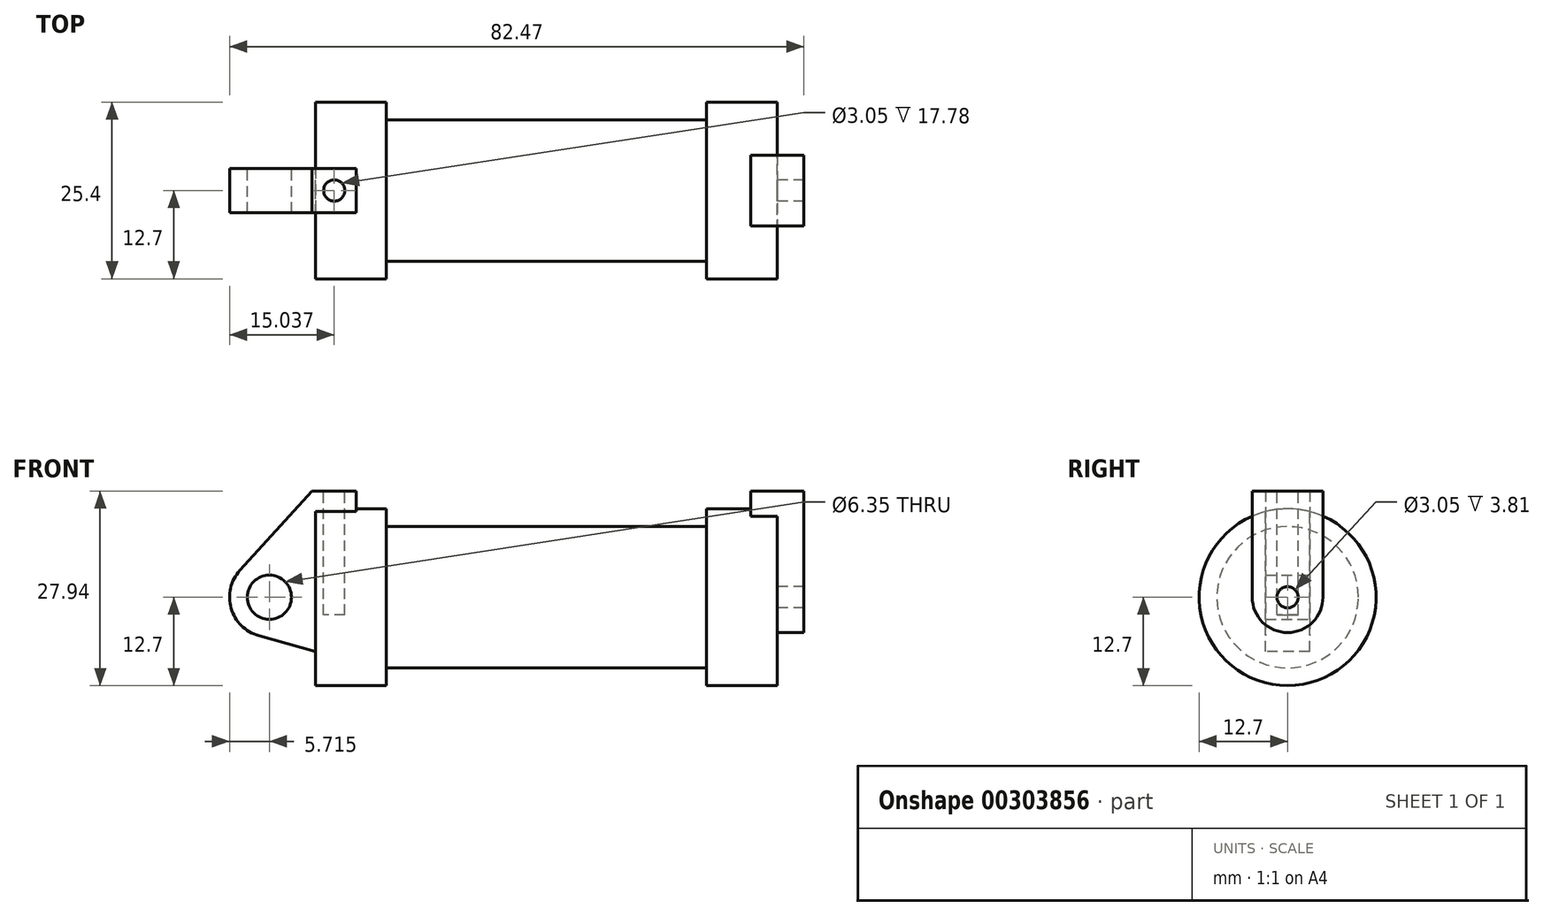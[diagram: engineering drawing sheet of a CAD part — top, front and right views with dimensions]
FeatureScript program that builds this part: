
annotation { "Feature Type Name" : "Feature", "Feature Type Description" : "" }
export const myFeature = defineFeature(function(context is Context, id is Id, definition is map)
    precondition{}
    {
        {
            var Q0;
            Q0=qCreatedBy(makeId("Front.planeOp"),FACE);
            var sketch = newSketch(context, id + "F0", { "sketchPlane" : qUnion([Q0])});
            skLineSegment(sketch, "E0", {"start": v(0, 0) * mm, "end": v(0, 12.7) * mm});
            skLineSegment(sketch, "E1", {"start": v(0, 12.7) * mm, "end": v(10.16, 12.7) * mm});
            skLineSegment(sketch, "E2", {"start": v(10.16, 12.7) * mm, "end": v(10.16, 10.16) * mm});
            skLineSegment(sketch, "E3", {"start": v(10.16, 10.16) * mm, "end": v(56.13, 10.16) * mm});
            skLineSegment(sketch, "E4", {"start": v(56.13, 10.16) * mm, "end": v(56.13, 12.7) * mm});
            skLineSegment(sketch, "E5", {"start": v(56.13, 12.7) * mm, "end": v(66.3, 12.7) * mm});
            skLineSegment(sketch, "E6", {"start": v(66.3, 12.7) * mm, "end": v(66.3, 0) * mm});
            skLineSegment(sketch, "E7", {"start": v(66.3, 0) * mm, "end": v(0, 0) * mm});
            skLineSegment(sketch, "E8", {"start": v(5.84, 15.24) * mm, "end": v(-0.5, 15.24) * mm});
            skLineSegment(sketch, "E9", {"start": v(-0.5, 15.24) * mm, "end": v(-10.88, 3.85) * mm});
            skLineSegment(sketch, "E10", {"start": v(0, 0) * mm, "end": v(-6.65, 0) * mm});
            skCircle(sketch, "E11", {"center": v(-6.65, 0) * mm, "radius": 5.72 * mm});
            skCircle(sketch, "E12", {"center": v(-6.65, 0) * mm, "radius": 3.18 * mm});
            skLineSegment(sketch, "E13", {"start": v(5.84, 15.24) * mm, "end": v(5.84, -9.4) * mm});
            skLineSegment(sketch, "E14", {"start": v(5.84, -9.4) * mm, "end": v(-8.18, -5.5) * mm});
            skSolve(sketch);
        }
        {
            var Q0;
            {var subQ0=sQuery(id+"F0.wireOp",EDGE,"E2");Q0=makeQuery(id+"F0.imprint","IMPRINT",FACE,{"disambiguationData":[TD([[makeQuery(id+"F0.imprint","IMPRINT",EDGE,{"derivedFrom":subQ0}),-1.0]])]});}
            var Q1;
            Q1=sQuery(id+"F0.wireOp",EDGE,"E7");
            revolve(context, id + "F1", {"entities" : qUnion([Q0]), "axis" : qUnion([Q1]), "revolveType" : RevolveType.FULL});
        }
        {
            var Q0;
            {var subQ0=sQuery(id+"F0.wireOp",EDGE,"E14");Q0=makeQuery(id+"F0.imprint","IMPRINT",FACE,{"disambiguationData":[TD([[makeQuery(id+"F0.imprint","IMPRINT",EDGE,{"derivedFrom":subQ0}),-1.0]])]});}
            var Q1;
            {var subQ5=sQuery(id+"F0.wireOp",EDGE,"E12");Q1=makeQuery(id+"F0.imprint","IMPRINT",FACE,{"disambiguationData":[TD([[makeQuery(id+"F0.imprint","IMPRINT",EDGE,{"derivedFrom":subQ5}),-1.0]])]});}
            var Q2;
            {var subQ1=sQuery(id+"F0.wireOp",EDGE,"E0");Q2=makeQuery(id+"F0.imprint","IMPRINT",FACE,{"disambiguationData":[TD([[makeQuery(id+"F0.imprint","IMPRINT",EDGE,{"derivedFrom":subQ1}),1.0]])]});}
            var Q3;
            {var subQ0=sQuery(id+"F0.wireOp",EDGE,"E0");Q3=makeQuery(id+"F0.imprint","IMPRINT",FACE,{"disambiguationData":[TD([[makeQuery(id+"F0.imprint","IMPRINT",EDGE,{"derivedFrom":subQ0}),-1.0]])]});}
            extrude(context, id + "F2", {"entities" : qUnion([Q0, Q1, Q2, Q3]), "operationType" : NewBodyOperationType.ADD, "endBound" : BoundingType.SYMMETRIC, "depth" : 6.35 * mm});
        }
        {
            var Q0;
            {var subQ0=sQuery(id+"F0.wireOp",EDGE,"E0");Q0=makeQuery(id+"F0.imprint","IMPRINT",FACE,{"disambiguationData":[TD([[makeQuery(id+"F0.imprint","IMPRINT",EDGE,{"derivedFrom":subQ0}),-1.0]])]});}
            var Q1;
            Q1=sQuery(id+"F0.wireOp",EDGE,"E7");
            revolve(context, id + "F3", {"operationType" : NewBodyOperationType.ADD, "entities" : qUnion([Q0]), "axis" : qUnion([Q1]), "revolveType" : RevolveType.FULL});
        }
        {
            var Q0;
            Q0=makeQuery(id+"F1.opRevolve","SWEPT_FACE",FACE,{"disambiguationData":[OSD([sQuery(id+"F0.wireOp",EDGE,"E6")])]});
            var sketch = newSketch(context, id + "F4", { "sketchPlane" : qUnion([Q0])});
            skCircle(sketch, "E15", {"center": v(0, 0) * mm, "radius": 5.08 * mm});
            skCircle(sketch, "E16", {"center": v(0, 0) * mm, "radius": 1.52 * mm});
            skLineSegment(sketch, "E17", {"start": v(5.08, 0) * mm, "end": v(5.08, 15.24) * mm});
            skLineSegment(sketch, "E18", {"start": v(-5.08, 0) * mm, "end": v(-5.08, 15.24) * mm});
            skLineSegment(sketch, "E19", {"start": v(-5.08, 15.24) * mm, "end": v(5.08, 15.24) * mm});
            skSolve(sketch);
        }
        {
            var Q0;
            Q0=makeQuery(id+"F4.imprint","IMPRINT",FACE,{"disambiguationData":[TD([[makeQuery(id+"F4.imprint","IMPRINT",EDGE,{"derivedFrom":sQuery(id+"F4.wireOp",EDGE,"E16")}),-1.0]])]});
            var Q1;
            {var subQ0=sQuery(id+"F4.wireOp",EDGE,"E17");var subQ1=sQuery(id+"F4.wireOp",EDGE,"E15");var subQ2=makeQuery(id+"F4.imprint","INTERSECT",VERTEX,{"derivedFrom":[subQ1,subQ0]});Q1=makeQuery(id+"F4.imprint","IMPRINT",FACE,{"disambiguationData":[TD([[makeQuery(id+"F4.imprint","IMPRINT",EDGE,{"disambiguationData":[TD([[subQ2,-1.0]])],"derivedFrom":subQ1}),-1.0]])]});}
            var Q2;
            {var subQ0=sQuery(id+"F4.wireOp",EDGE,"E19");Q2=makeQuery(id+"F4.imprint","IMPRINT",FACE,{"disambiguationData":[TD([[makeQuery(id+"F4.imprint","IMPRINT",EDGE,{"derivedFrom":subQ0}),-1.0]])]});}
            extrude(context, id + "F5", {"entities" : qUnion([Q0, Q1, Q2]), "operationType" : NewBodyOperationType.ADD, "endBound" : BoundingType.SYMMETRIC, "depth" : 7.62 * mm});
        }
        {
            var Q0;
            Q0=makeQuery(id+"F5.opExtrude","SWEPT_FACE",FACE,{"disambiguationData":[OSD([sQuery(id+"F4.wireOp",EDGE,"E19")])]});
            var sketch = newSketch(context, id + "F6", { "sketchPlane" : qUnion([Q0])});
            skCircle(sketch, "E20", {"center": v(66.3, 0) * mm, "radius": 1.52 * mm});
            skPoint(sketch, "E20.centerSnap0", {"position": v(66.3, 5.08) * mm});
            skPoint(sketch, "E20.centerSnap1", {"position": v(62.48, 0) * mm});
            skSolve(sketch);
        }
        {
            var Q0;
            Q0=makeQuery(id+"F2.opExtrude","SWEPT_FACE",FACE,{"disambiguationData":[OSD([sQuery(id+"F0.wireOp",EDGE,"E8")])]});
            var sketch = newSketch(context, id + "F7", { "sketchPlane" : qUnion([Q0])});
            skCircle(sketch, "E21", {"center": v(2.67, 0) * mm, "radius": 1.52 * mm});
            skPoint(sketch, "E21.centerSnap0", {"position": v(5.84, 0) * mm});
            skPoint(sketch, "E21.centerSnap1", {"position": v(2.67, 3.18) * mm});
            skSolve(sketch);
        }
        {
            var Q0;
            Q0=sQuery(id+"F7.wireOp",EDGE,"E21");
            var Q1;
            Q1 = qConstructionFilter(qBodyType(qCreatedBy(id + "F6" ,EDGE), BodyType.WIRE), ConstructionObject.NO);
            extrude(context, id + "F8", {"bodyType" : ToolBodyType.SURFACE, "surfaceEntities" : qUnion([Q0, Q1]), "oppositeDirection" : true, "depth" : 17.78 * mm});
        }
        {
            var Q0;
            Q0 = qSketchRegion(id + "F7", true);
            extrude(context, id + "F9", {"entities" : qUnion([Q0]), "operationType" : NewBodyOperationType.REMOVE, "oppositeDirection" : true, "depth" : 17.78 * mm});
        }
    });
